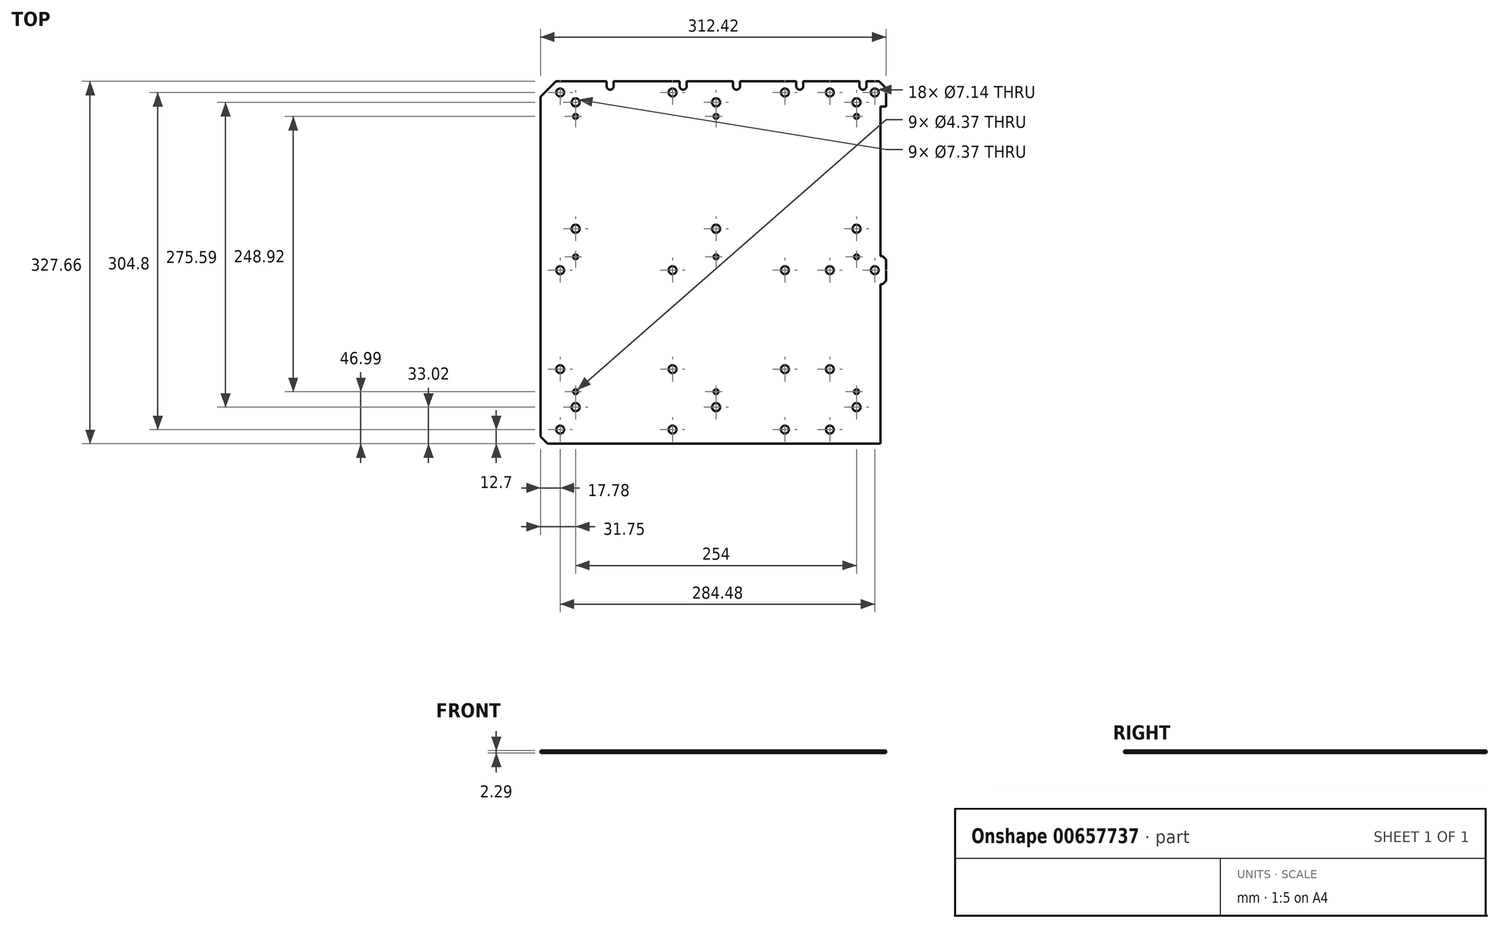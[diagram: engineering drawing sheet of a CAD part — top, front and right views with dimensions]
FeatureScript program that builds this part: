
annotation { "Feature Type Name" : "Feature", "Feature Type Description" : "" }
export const myFeature = defineFeature(function(context is Context, id is Id, definition is map)
    precondition{}
    {
        {
            var Q0;
            Q0=qCreatedBy(makeId("Top.planeOp"),FACE);
            var sketch = newSketch(context, id + "F0", { "sketchPlane" : qUnion([Q0])});
            skLineSegment(sketch, "E0.bottom", {"start": v(156.21, 163.83) * mm, "end": v(-156.2, 163.83) * mm});
            skLineSegment(sketch, "E0.top", {"start": v(156.2, -163.83) * mm, "end": v(-156.21, -163.83) * mm});
            skLineSegment(sketch, "E0.left", {"start": v(156.21, 163.83) * mm, "end": v(156.2, -163.83) * mm});
            skLineSegment(sketch, "E0.right", {"start": v(-156.2, 163.83) * mm, "end": v(-156.21, -163.83) * mm});
            skPoint(sketch, "E0.middle", {"position": v(0, 0) * mm});
            skPoint(sketch, "E1", {"position": v(-138.43, 153.67) * mm});
            skPoint(sketch, "E2", {"position": v(-36.83, 153.67) * mm});
            skPoint(sketch, "E3", {"position": v(64.77, 153.67) * mm});
            skPoint(sketch, "E4", {"position": v(105.41, 153.67) * mm});
            skPoint(sketch, "E5", {"position": v(146.05, 153.67) * mm});
            skPoint(sketch, "E6", {"position": v(-124.46, 144.78) * mm});
            skPoint(sketch, "E7", {"position": v(2.54, 144.78) * mm});
            skPoint(sketch, "E8", {"position": v(129.54, 144.78) * mm});
            skPoint(sketch, "E9", {"position": v(-124.46, 132.08) * mm});
            skPoint(sketch, "E10", {"position": v(2.54, 132.08) * mm});
            skPoint(sketch, "E11", {"position": v(129.54, 132.08) * mm});
            skPoint(sketch, "E12", {"position": v(-124.46, 30.48) * mm});
            skPoint(sketch, "E13", {"position": v(-124.46, 5.08) * mm});
            skPoint(sketch, "E14", {"position": v(-124.46, -116.84) * mm});
            skPoint(sketch, "E15", {"position": v(-124.46, -130.8) * mm});
            skPoint(sketch, "E16", {"position": v(2.54, 30.48) * mm});
            skPoint(sketch, "E17", {"position": v(2.54, 5.08) * mm});
            skPoint(sketch, "E18", {"position": v(2.54, -116.84) * mm});
            skPoint(sketch, "E19", {"position": v(2.54, -130.8) * mm});
            skPoint(sketch, "E20", {"position": v(129.54, 30.48) * mm});
            skPoint(sketch, "E21", {"position": v(129.54, 5.08) * mm});
            skPoint(sketch, "E22", {"position": v(129.54, -116.84) * mm});
            skPoint(sketch, "E23", {"position": v(129.54, -130.8) * mm});
            skPoint(sketch, "E24", {"position": v(-138.43, -6.98) * mm});
            skPoint(sketch, "E25", {"position": v(-138.43, -96.52) * mm});
            skPoint(sketch, "E26", {"position": v(-36.83, -6.98) * mm});
            skPoint(sketch, "E27", {"position": v(-36.83, -96.52) * mm});
            skPoint(sketch, "E28", {"position": v(-138.43, -151.13) * mm});
            skPoint(sketch, "E29", {"position": v(-36.83, -151.13) * mm});
            skPoint(sketch, "E30", {"position": v(64.77, -6.98) * mm});
            skPoint(sketch, "E31", {"position": v(64.77, -96.52) * mm});
            skPoint(sketch, "E32", {"position": v(64.77, -151.13) * mm});
            skPoint(sketch, "E33", {"position": v(105.41, -6.98) * mm});
            skPoint(sketch, "E34", {"position": v(105.41, -96.52) * mm});
            skPoint(sketch, "E35", {"position": v(105.41, -151.13) * mm});
            skPoint(sketch, "E36", {"position": v(146.05, -6.98) * mm});
            skCircle(sketch, "E37", {"center": v(-138.43, 153.67) * mm, "radius": 3.57 * mm});
            skCircle(sketch, "E38", {"center": v(-36.83, 153.67) * mm, "radius": 3.57 * mm});
            skCircle(sketch, "E39", {"center": v(64.77, 153.67) * mm, "radius": 3.57 * mm});
            skCircle(sketch, "E40", {"center": v(105.41, 153.67) * mm, "radius": 3.57 * mm});
            skCircle(sketch, "E41", {"center": v(146.05, 153.67) * mm, "radius": 3.57 * mm});
            skCircle(sketch, "E42", {"center": v(-138.43, -6.98) * mm, "radius": 3.57 * mm});
            skCircle(sketch, "E43", {"center": v(-138.43, -96.52) * mm, "radius": 3.57 * mm});
            skCircle(sketch, "E44", {"center": v(-138.43, -151.13) * mm, "radius": 3.57 * mm});
            skCircle(sketch, "E45", {"center": v(-36.83, -151.13) * mm, "radius": 3.57 * mm});
            skCircle(sketch, "E46", {"center": v(64.77, -151.13) * mm, "radius": 3.57 * mm});
            skCircle(sketch, "E47", {"center": v(105.41, -151.13) * mm, "radius": 3.57 * mm});
            skCircle(sketch, "E48", {"center": v(105.41, -96.52) * mm, "radius": 3.57 * mm});
            skCircle(sketch, "E49", {"center": v(64.77, -96.52) * mm, "radius": 3.57 * mm});
            skCircle(sketch, "E50", {"center": v(-36.83, -96.52) * mm, "radius": 3.57 * mm});
            skCircle(sketch, "E51", {"center": v(-36.83, -6.98) * mm, "radius": 3.57 * mm});
            skCircle(sketch, "E52", {"center": v(64.77, -6.98) * mm, "radius": 3.57 * mm});
            skCircle(sketch, "E53", {"center": v(105.41, -6.98) * mm, "radius": 3.57 * mm});
            skCircle(sketch, "E54", {"center": v(146.05, -6.98) * mm, "radius": 3.57 * mm});
            skCircle(sketch, "E55", {"center": v(-124.46, 144.78) * mm, "radius": 3.68 * mm});
            skCircle(sketch, "E56", {"center": v(2.54, 144.78) * mm, "radius": 3.68 * mm});
            skCircle(sketch, "E57", {"center": v(129.54, 144.78) * mm, "radius": 3.68 * mm});
            skCircle(sketch, "E58", {"center": v(129.54, 30.48) * mm, "radius": 3.68 * mm});
            skCircle(sketch, "E59", {"center": v(2.54, 30.48) * mm, "radius": 3.68 * mm});
            skCircle(sketch, "E60", {"center": v(-124.46, 30.48) * mm, "radius": 3.68 * mm});
            skCircle(sketch, "E61", {"center": v(-124.46, -130.8) * mm, "radius": 3.68 * mm});
            skCircle(sketch, "E62", {"center": v(2.54, -130.8) * mm, "radius": 3.68 * mm});
            skCircle(sketch, "E63", {"center": v(129.54, -130.8) * mm, "radius": 3.68 * mm});
            skCircle(sketch, "E64", {"center": v(-124.46, 132.08) * mm, "radius": 2.18 * mm});
            skCircle(sketch, "E65", {"center": v(2.54, 132.08) * mm, "radius": 2.18 * mm});
            skCircle(sketch, "E66", {"center": v(129.54, 132.08) * mm, "radius": 2.18 * mm});
            skCircle(sketch, "E67", {"center": v(-124.46, 5.08) * mm, "radius": 2.18 * mm});
            skCircle(sketch, "E68", {"center": v(2.54, 5.08) * mm, "radius": 2.18 * mm});
            skCircle(sketch, "E69", {"center": v(129.54, 5.08) * mm, "radius": 2.18 * mm});
            skCircle(sketch, "E70", {"center": v(129.54, -116.84) * mm, "radius": 2.18 * mm});
            skCircle(sketch, "E71", {"center": v(2.54, -116.84) * mm, "radius": 2.18 * mm});
            skCircle(sketch, "E72", {"center": v(-124.46, -116.84) * mm, "radius": 2.18 * mm});
            skSolve(sketch);
        }
        {
            var Q0;
            Q0=makeQuery(id+"F0.imprint","IMPRINT",FACE,{"disambiguationData":[TD([[makeQuery(id+"F0.imprint","IMPRINT",EDGE,{"derivedFrom":sQuery(id+"F0.wireOp",EDGE,"E0.bottom")}),1.0]])]});
            extrude(context, id + "F1", {"entities" : qUnion([Q0]), "depth" : 2.3 * mm, "offsetDistance" : 25.4 * mm});
        }
        {
            var Q0;
            Q0=makeQuery(id+"F1.opExtrude","CAP_FACE",FACE,{"disambiguationData":[OSD([sQuery(id+"F0.wireOp",EDGE,"E0.bottom"),sQuery(id+"F0.wireOp",EDGE,"E0.top"),sQuery(id+"F0.wireOp",EDGE,"E0.left"),sQuery(id+"F0.wireOp",EDGE,"E0.right"),sQuery(id+"F0.wireOp",EDGE,"E37"),sQuery(id+"F0.wireOp",EDGE,"E38"),sQuery(id+"F0.wireOp",EDGE,"E39"),sQuery(id+"F0.wireOp",EDGE,"E40"),sQuery(id+"F0.wireOp",EDGE,"E41"),sQuery(id+"F0.wireOp",EDGE,"E42"),sQuery(id+"F0.wireOp",EDGE,"E43"),sQuery(id+"F0.wireOp",EDGE,"E44"),sQuery(id+"F0.wireOp",EDGE,"E45"),sQuery(id+"F0.wireOp",EDGE,"E46"),sQuery(id+"F0.wireOp",EDGE,"E47"),sQuery(id+"F0.wireOp",EDGE,"E48"),sQuery(id+"F0.wireOp",EDGE,"E49"),sQuery(id+"F0.wireOp",EDGE,"E50"),sQuery(id+"F0.wireOp",EDGE,"E51"),sQuery(id+"F0.wireOp",EDGE,"E52"),sQuery(id+"F0.wireOp",EDGE,"E53"),sQuery(id+"F0.wireOp",EDGE,"E54"),sQuery(id+"F0.wireOp",EDGE,"E55"),sQuery(id+"F0.wireOp",EDGE,"E56"),sQuery(id+"F0.wireOp",EDGE,"E57"),sQuery(id+"F0.wireOp",EDGE,"E58"),sQuery(id+"F0.wireOp",EDGE,"E59"),sQuery(id+"F0.wireOp",EDGE,"E60"),sQuery(id+"F0.wireOp",EDGE,"E61"),sQuery(id+"F0.wireOp",EDGE,"E62"),sQuery(id+"F0.wireOp",EDGE,"E63"),sQuery(id+"F0.wireOp",EDGE,"E64"),sQuery(id+"F0.wireOp",EDGE,"E65"),sQuery(id+"F0.wireOp",EDGE,"E66"),sQuery(id+"F0.wireOp",EDGE,"E67"),sQuery(id+"F0.wireOp",EDGE,"E68"),sQuery(id+"F0.wireOp",EDGE,"E69"),sQuery(id+"F0.wireOp",EDGE,"E70"),sQuery(id+"F0.wireOp",EDGE,"E71"),sQuery(id+"F0.wireOp",EDGE,"E72")])],"isStart":false});
            var sketch = newSketch(context, id + "F2", { "sketchPlane" : qUnion([Q0])});
            skPoint(sketch, "E73", {"position": v(-93.22, 163.83) * mm});
            skPoint(sketch, "E74", {"position": v(-27.18, 163.83) * mm});
            skPoint(sketch, "E75", {"position": v(21.08, 163.83) * mm});
            skPoint(sketch, "E76", {"position": v(78.23, 163.83) * mm});
            skPoint(sketch, "E77", {"position": v(135.38, 163.83) * mm});
            skLineSegment(sketch, "E78.bottom", {"start": v(-90.04, 168.28) * mm, "end": v(-96.4, 168.28) * mm});
            skLineSegment(sketch, "E78.top", {"start": v(-90.04, 159.38) * mm, "end": v(-96.4, 159.38) * mm});
            skLineSegment(sketch, "E78.left", {"start": v(-90.04, 168.28) * mm, "end": v(-90.04, 159.38) * mm});
            skLineSegment(sketch, "E78.right", {"start": v(-96.4, 168.28) * mm, "end": v(-96.4, 159.39) * mm});
            skLineSegment(sketch, "E79.bottom", {"start": v(-24, 168.28) * mm, "end": v(-30.35, 168.28) * mm});
            skLineSegment(sketch, "E79.top", {"start": v(-24, 159.39) * mm, "end": v(-30.35, 159.39) * mm});
            skLineSegment(sketch, "E79.left", {"start": v(-24, 168.28) * mm, "end": v(-24, 159.39) * mm});
            skLineSegment(sketch, "E79.right", {"start": v(-30.35, 168.28) * mm, "end": v(-30.35, 159.39) * mm});
            skLineSegment(sketch, "E80.bottom", {"start": v(17.9, 168.28) * mm, "end": v(24.26, 168.28) * mm});
            skLineSegment(sketch, "E80.top", {"start": v(17.9, 159.38) * mm, "end": v(24.26, 159.38) * mm});
            skLineSegment(sketch, "E80.left", {"start": v(17.9, 168.28) * mm, "end": v(17.9, 159.38) * mm});
            skLineSegment(sketch, "E80.right", {"start": v(24.26, 168.28) * mm, "end": v(24.26, 159.38) * mm});
            skLineSegment(sketch, "E81.bottom", {"start": v(75.06, 168.28) * mm, "end": v(81.4, 168.28) * mm});
            skLineSegment(sketch, "E81.top", {"start": v(75.06, 159.38) * mm, "end": v(81.4, 159.38) * mm});
            skLineSegment(sketch, "E81.left", {"start": v(75.06, 168.28) * mm, "end": v(75.06, 159.38) * mm});
            skLineSegment(sketch, "E81.right", {"start": v(81.4, 168.28) * mm, "end": v(81.4, 159.38) * mm});
            skLineSegment(sketch, "E82.bottom", {"start": v(132.2, 168.28) * mm, "end": v(138.56, 168.28) * mm});
            skLineSegment(sketch, "E82.top", {"start": v(132.2, 159.38) * mm, "end": v(138.56, 159.38) * mm});
            skLineSegment(sketch, "E82.left", {"start": v(132.2, 168.28) * mm, "end": v(132.2, 159.38) * mm});
            skLineSegment(sketch, "E82.right", {"start": v(138.56, 168.28) * mm, "end": v(138.56, 159.38) * mm});
            skArc(sketch, "E83", {"start": v(-96.4, 159.39) * mm, "mid": v(-93.22, 156.21) * mm, "end": v(-90.04, 159.38) * mm});
            skArc(sketch, "E84", {"start": v(-30.35, 159.39) * mm, "mid": v(-27.18, 156.21) * mm, "end": v(-24, 159.39) * mm});
            skArc(sketch, "E85", {"start": v(17.9, 159.38) * mm, "mid": v(21.08, 156.2) * mm, "end": v(24.26, 159.38) * mm});
            skArc(sketch, "E86", {"start": v(75.06, 159.38) * mm, "mid": v(78.23, 156.21) * mm, "end": v(81.4, 159.38) * mm});
            skArc(sketch, "E87", {"start": v(132.2, 159.38) * mm, "mid": v(135.38, 156.21) * mm, "end": v(138.56, 159.38) * mm});
            skPoint(sketch, "E88", {"position": v(156.21, 140.97) * mm});
            skPoint(sketch, "E89", {"position": v(156.21, 5.71) * mm});
            skPoint(sketch, "E90", {"position": v(156.21, -19.69) * mm});
            skLineSegment(sketch, "E91.bottom", {"start": v(156.21, 140.97) * mm, "end": v(151.13, 140.97) * mm});
            skLineSegment(sketch, "E91.top", {"start": v(156.21, 5.71) * mm, "end": v(151.13, 5.71) * mm});
            skLineSegment(sketch, "E91.left", {"start": v(156.21, 140.97) * mm, "end": v(156.21, 5.71) * mm});
            skLineSegment(sketch, "E91.right", {"start": v(151.13, 140.97) * mm, "end": v(151.13, 5.71) * mm});
            skLineSegment(sketch, "E92.bottom", {"start": v(156.21, -19.69) * mm, "end": v(151.13, -19.69) * mm});
            skLineSegment(sketch, "E92.top", {"start": v(156.21, -163.83) * mm, "end": v(151.13, -163.83) * mm});
            skLineSegment(sketch, "E92.left", {"start": v(156.21, -19.69) * mm, "end": v(156.21, -163.83) * mm});
            skLineSegment(sketch, "E92.right", {"start": v(151.13, -19.69) * mm, "end": v(151.13, -163.83) * mm});
            skSolve(sketch);
        }
        {
            var Q0;
            Q0=makeQuery(id+"F2.imprint","IMPRINT",FACE,{"disambiguationData":[TD([[makeQuery(id+"F2.imprint","IMPRINT",EDGE,{"derivedFrom":sQuery(id+"F2.wireOp",EDGE,"E78.top")}),1.0]])]});
            var Q1;
            {var subQ0=sQuery(id+"F2.wireOp",EDGE,"E78.top");Q1=makeQuery(id+"F2.imprint","IMPRINT",FACE,{"disambiguationData":[TD([[makeQuery(id+"F2.imprint","IMPRINT",EDGE,{"derivedFrom":subQ0}),-1.0]])]});}
            var Q2;
            {var subQ0=sQuery(id+"F2.wireOp",EDGE,"E78.bottom");Q2=makeQuery(id+"F2.imprint","IMPRINT",FACE,{"disambiguationData":[TD([[makeQuery(id+"F2.imprint","IMPRINT",EDGE,{"derivedFrom":subQ0}),1.0]])]});}
            var Q3;
            {var subQ0=sQuery(id+"F2.wireOp",EDGE,"E79.bottom");Q3=makeQuery(id+"F2.imprint","IMPRINT",FACE,{"disambiguationData":[TD([[makeQuery(id+"F2.imprint","IMPRINT",EDGE,{"derivedFrom":subQ0}),1.0]])]});}
            var Q4;
            {var subQ0=sQuery(id+"F2.wireOp",EDGE,"E79.top");Q4=makeQuery(id+"F2.imprint","IMPRINT",FACE,{"disambiguationData":[TD([[makeQuery(id+"F2.imprint","IMPRINT",EDGE,{"derivedFrom":subQ0}),-1.0]])]});}
            var Q5;
            Q5=makeQuery(id+"F2.imprint","IMPRINT",FACE,{"disambiguationData":[TD([[makeQuery(id+"F2.imprint","IMPRINT",EDGE,{"derivedFrom":sQuery(id+"F2.wireOp",EDGE,"E79.top")}),1.0]])]});
            var Q6;
            {var subQ0=sQuery(id+"F2.wireOp",EDGE,"E80.bottom");Q6=makeQuery(id+"F2.imprint","IMPRINT",FACE,{"disambiguationData":[TD([[makeQuery(id+"F2.imprint","IMPRINT",EDGE,{"derivedFrom":subQ0}),-1.0]])]});}
            var Q7;
            {var subQ0=sQuery(id+"F2.wireOp",EDGE,"E80.top");Q7=makeQuery(id+"F2.imprint","IMPRINT",FACE,{"disambiguationData":[TD([[makeQuery(id+"F2.imprint","IMPRINT",EDGE,{"derivedFrom":subQ0}),1.0]])]});}
            var Q8;
            Q8=makeQuery(id+"F2.imprint","IMPRINT",FACE,{"disambiguationData":[TD([[makeQuery(id+"F2.imprint","IMPRINT",EDGE,{"derivedFrom":sQuery(id+"F2.wireOp",EDGE,"E80.top")}),-1.0]])]});
            var Q9;
            {var subQ0=sQuery(id+"F2.wireOp",EDGE,"E81.bottom");Q9=makeQuery(id+"F2.imprint","IMPRINT",FACE,{"disambiguationData":[TD([[makeQuery(id+"F2.imprint","IMPRINT",EDGE,{"derivedFrom":subQ0}),-1.0]])]});}
            var Q10;
            {var subQ0=sQuery(id+"F2.wireOp",EDGE,"E81.top");Q10=makeQuery(id+"F2.imprint","IMPRINT",FACE,{"disambiguationData":[TD([[makeQuery(id+"F2.imprint","IMPRINT",EDGE,{"derivedFrom":subQ0}),1.0]])]});}
            var Q11;
            Q11=makeQuery(id+"F2.imprint","IMPRINT",FACE,{"disambiguationData":[TD([[makeQuery(id+"F2.imprint","IMPRINT",EDGE,{"derivedFrom":sQuery(id+"F2.wireOp",EDGE,"E81.top")}),-1.0]])]});
            var Q12;
            {var subQ0=sQuery(id+"F2.wireOp",EDGE,"E82.bottom");Q12=makeQuery(id+"F2.imprint","IMPRINT",FACE,{"disambiguationData":[TD([[makeQuery(id+"F2.imprint","IMPRINT",EDGE,{"derivedFrom":subQ0}),-1.0]])]});}
            var Q13;
            {var subQ0=sQuery(id+"F2.wireOp",EDGE,"E82.top");Q13=makeQuery(id+"F2.imprint","IMPRINT",FACE,{"disambiguationData":[TD([[makeQuery(id+"F2.imprint","IMPRINT",EDGE,{"derivedFrom":subQ0}),1.0]])]});}
            var Q14;
            Q14=makeQuery(id+"F2.imprint","IMPRINT",FACE,{"disambiguationData":[TD([[makeQuery(id+"F2.imprint","IMPRINT",EDGE,{"derivedFrom":sQuery(id+"F2.wireOp",EDGE,"E82.top")}),-1.0]])]});
            var Q15;
            Q15=makeQuery(id+"F2.imprint","IMPRINT",FACE,{"disambiguationData":[TD([[makeQuery(id+"F2.imprint","IMPRINT",EDGE,{"derivedFrom":sQuery(id+"F2.wireOp",EDGE,"E91.bottom")}),1.0]])]});
            var Q16;
            Q16=makeQuery(id+"F2.imprint","IMPRINT",FACE,{"disambiguationData":[TD([[makeQuery(id+"F2.imprint","IMPRINT",EDGE,{"derivedFrom":sQuery(id+"F2.wireOp",EDGE,"E92.bottom")}),1.0]])]});
            extrude(context, id + "F3", {"entities" : qUnion([Q0, Q1, Q2, Q3, Q4, Q5, Q6, Q7, Q8, Q9, Q10, Q11, Q12, Q13, Q14, Q15, Q16]), "operationType" : NewBodyOperationType.REMOVE, "endBound" : BoundingType.THROUGH_ALL, "oppositeDirection" : true, "depth" : 25.4 * mm, "offsetDistance" : 25.4 * mm});
        }
        {
            var Q0;
            Q0=makeQuery(id+"F1.opExtrude","SWEPT_EDGE",EDGE,{"disambiguationData":[OSD([sQuery(id+"F0.wireOp",EDGE,"E0.bottom"),sQuery(id+"F0.wireOp",EDGE,"E0.right")])]});
            chamfer(context, id + "F4", {"entities" : qUnion([Q0]), "width" : 13.97 * mm, "tangentPropagation" : true});
        }
        {
            var Q0;
            Q0=makeQuery(id+"F1.opExtrude","SWEPT_EDGE",EDGE,{"disambiguationData":[OSD([sQuery(id+"F0.wireOp",EDGE,"E0.top"),sQuery(id+"F0.wireOp",EDGE,"E0.right")])]});
            var Q1;
            Q1=makeQuery(id+"F3.boolean.opBoolean","COPY",EDGE,{"derivedFrom":makeQuery(id+"F3.opExtrude","SWEPT_EDGE",EDGE,{"disambiguationData":[OSD([sQuery(id+"F0.wireOp",EDGE,"E0.top"),sQuery(id+"F2.wireOp",EDGE,"E92.top"),sQuery(id+"F2.wireOp",EDGE,"E92.right")])]})});
            var Q2;
            Q2=makeQuery(id+"F1.opExtrude","SWEPT_EDGE",EDGE,{"disambiguationData":[OSD([sQuery(id+"F0.wireOp",EDGE,"E0.bottom"),sQuery(id+"F0.wireOp",EDGE,"E0.left")])]});
            chamfer(context, id + "F5", {"entities" : qUnion([Q0, Q1, Q2]), "width" : 6.35 * mm, "tangentPropagation" : true});
        }
        {
            var Q0;
            Q0=makeQuery(id+"F3.boolean.opBoolean","COPY",EDGE,{"derivedFrom":makeQuery(id+"F3.opExtrude","SWEPT_EDGE",EDGE,{"disambiguationData":[OSD([sQuery(id+"F0.wireOp",EDGE,"E0.left"),sQuery(id+"F2.wireOp",EDGE,"E91.bottom"),sQuery(id+"F2.wireOp",EDGE,"E91.left")])]})});
            var Q1;
            Q1=makeQuery(id+"F3.boolean.opBoolean","COPY",EDGE,{"derivedFrom":makeQuery(id+"F3.opExtrude","SWEPT_EDGE",EDGE,{"disambiguationData":[OSD([sQuery(id+"F0.wireOp",EDGE,"E0.left"),sQuery(id+"F2.wireOp",EDGE,"E91.top"),sQuery(id+"F2.wireOp",EDGE,"E91.left")])]})});
            var Q2;
            Q2=makeQuery(id+"F3.boolean.opBoolean","COPY",EDGE,{"derivedFrom":makeQuery(id+"F3.opExtrude","SWEPT_EDGE",EDGE,{"disambiguationData":[OSD([sQuery(id+"F0.wireOp",EDGE,"E0.left"),sQuery(id+"F2.wireOp",EDGE,"E92.bottom"),sQuery(id+"F2.wireOp",EDGE,"E92.left")])]})});
            chamfer(context, id + "F6", {"entities" : qUnion([Q0, Q1, Q2]), "width" : 3.17 * mm, "tangentPropagation" : true});
        }
    });
